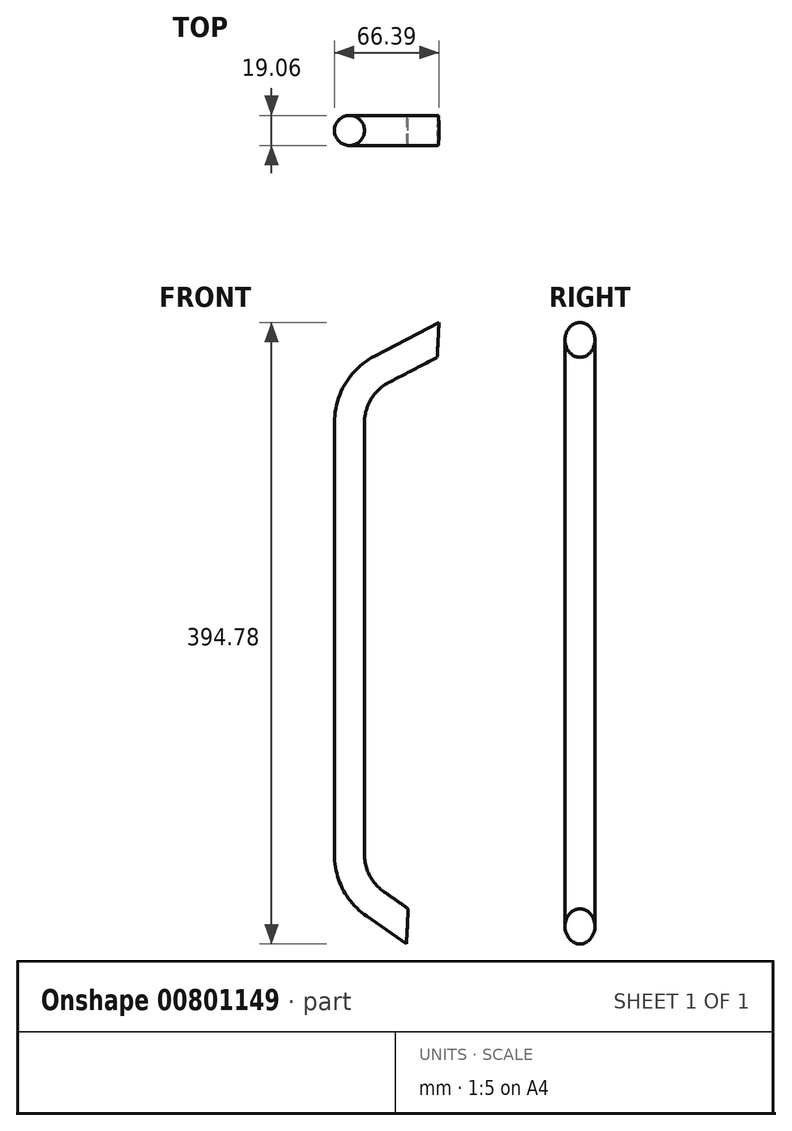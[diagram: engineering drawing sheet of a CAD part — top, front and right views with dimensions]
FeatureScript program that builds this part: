
annotation { "Feature Type Name" : "Feature", "Feature Type Description" : "" }
export const myFeature = defineFeature(function(context is Context, id is Id, definition is map)
    precondition{}
    {
        {
            var Q0;
            Q0=qCreatedBy(makeId("Front.planeOp"),FACE);
            var sketch = newSketch(context, id + "F0", { "sketchPlane" : qUnion([Q0])});
            skLineSegment(sketch, "E0", {"start": v(0, 0) * mm, "end": v(-25.37, 17.76) * mm});
            skLineSegment(sketch, "E1", {"start": v(-41.61, 48.97) * mm, "end": v(-41.61, 323.52) * mm});
            skLineSegment(sketch, "E2", {"start": v(-21.1, 357.31) * mm, "end": v(20.34, 378.9) * mm});
            skPoint(sketch, "E3.visualSharp", {"position": v(-41.61, 346.64) * mm});
            skArc(sketch, "E3.filletArc", {"start": v(-21.1, 357.31) * mm, "mid": v(-36.09, 343.28) * mm, "end": v(-41.61, 323.52) * mm});
            skPoint(sketch, "E4.visualSharp", {"position": v(-41.61, 29.14) * mm});
            skArc(sketch, "E4.filletArc", {"start": v(-41.61, 48.97) * mm, "mid": v(-37.3, 31.38) * mm, "end": v(-25.37, 17.76) * mm});
            skSolve(sketch);
        }
        {
            var Q0;
            Q0=sQuery(id+"F0.wireOp",EDGE,"E0");
            var Q1;
            Q1=sQuery(id+"F0.wireOp",VERTEX,"E0.start");
            cPlane(context, id + "F1", {"entities" : qUnion([Q0, Q1]), "cplaneType" : CPlaneType.LINE_POINT, "offset" : 25.4 * mm, "width" : 152.4 * mm, "height" : 152.4 * mm});
        }
        {
            var Q0;
            Q0=qCreatedBy(id+"F1.planeOp",FACE);
            var sketch = newSketch(context, id + "F2", { "sketchPlane" : qUnion([Q0])});
            skCircle(sketch, "E5", {"center": v(0, 0) * mm, "radius": 9.53 * mm});
            skSolve(sketch);
        }
        {
            var Q0;
            Q0=makeQuery(id+"F2.imprint","IMPRINT",FACE,{"disambiguationData":[TD([[makeQuery(id+"F2.imprint","IMPRINT",EDGE,{"derivedFrom":sQuery(id+"F2.wireOp",EDGE,"E5")}),1.0]])]});
            var Q1;
            Q1=sQuery(id+"F0.wireOp",EDGE,"E0");
            var Q2;
            Q2=sQuery(id+"F0.wireOp",EDGE,"E4.filletArc");
            var Q3;
            Q3=sQuery(id+"F0.wireOp",EDGE,"E1");
            var Q4;
            Q4=sQuery(id+"F0.wireOp",EDGE,"E3.filletArc");
            var Q5;
            Q5=sQuery(id+"F0.wireOp",EDGE,"E2");
            sweep(context, id + "F3", {"profiles" : qUnion([Q0]), "path" : qUnion([Q1, Q2, Q3, Q4, Q5])});
        }
        {
            var Q0;
            Q0=qCreatedBy(makeId("Front.planeOp"),FACE);
            var sketch = newSketch(context, id + "F4", { "sketchPlane" : qUnion([Q0])});
            skLineSegment(sketch, "E6", {"start": v(-5.46, -7.8) * mm, "end": v(15.33, 388.53) * mm});
            skLineSegment(sketch, "E7", {"start": v(34.38, 388.53) * mm, "end": v(13.59, -7.8) * mm});
            skLineSegment(sketch, "E8", {"start": v(13.59, -7.8) * mm, "end": v(-5.46, -7.8) * mm});
            skLineSegment(sketch, "E9", {"start": v(15.33, 388.53) * mm, "end": v(34.38, 388.53) * mm});
            skSolve(sketch);
        }
        {
            var Q0;
            Q0=makeQuery(id+"F4.imprint","IMPRINT",FACE,{"disambiguationData":[TD([[makeQuery(id+"F4.imprint","IMPRINT",EDGE,{"derivedFrom":sQuery(id+"F4.wireOp",EDGE,"E6")}),-1.0]])]});
            extrude(context, id + "F5", {"entities" : qUnion([Q0]), "operationType" : NewBodyOperationType.REMOVE, "endBound" : BoundingType.SYMMETRIC, "depth" : 25.4 * mm, "offsetDistance" : 25.4 * mm});
        }
    });
